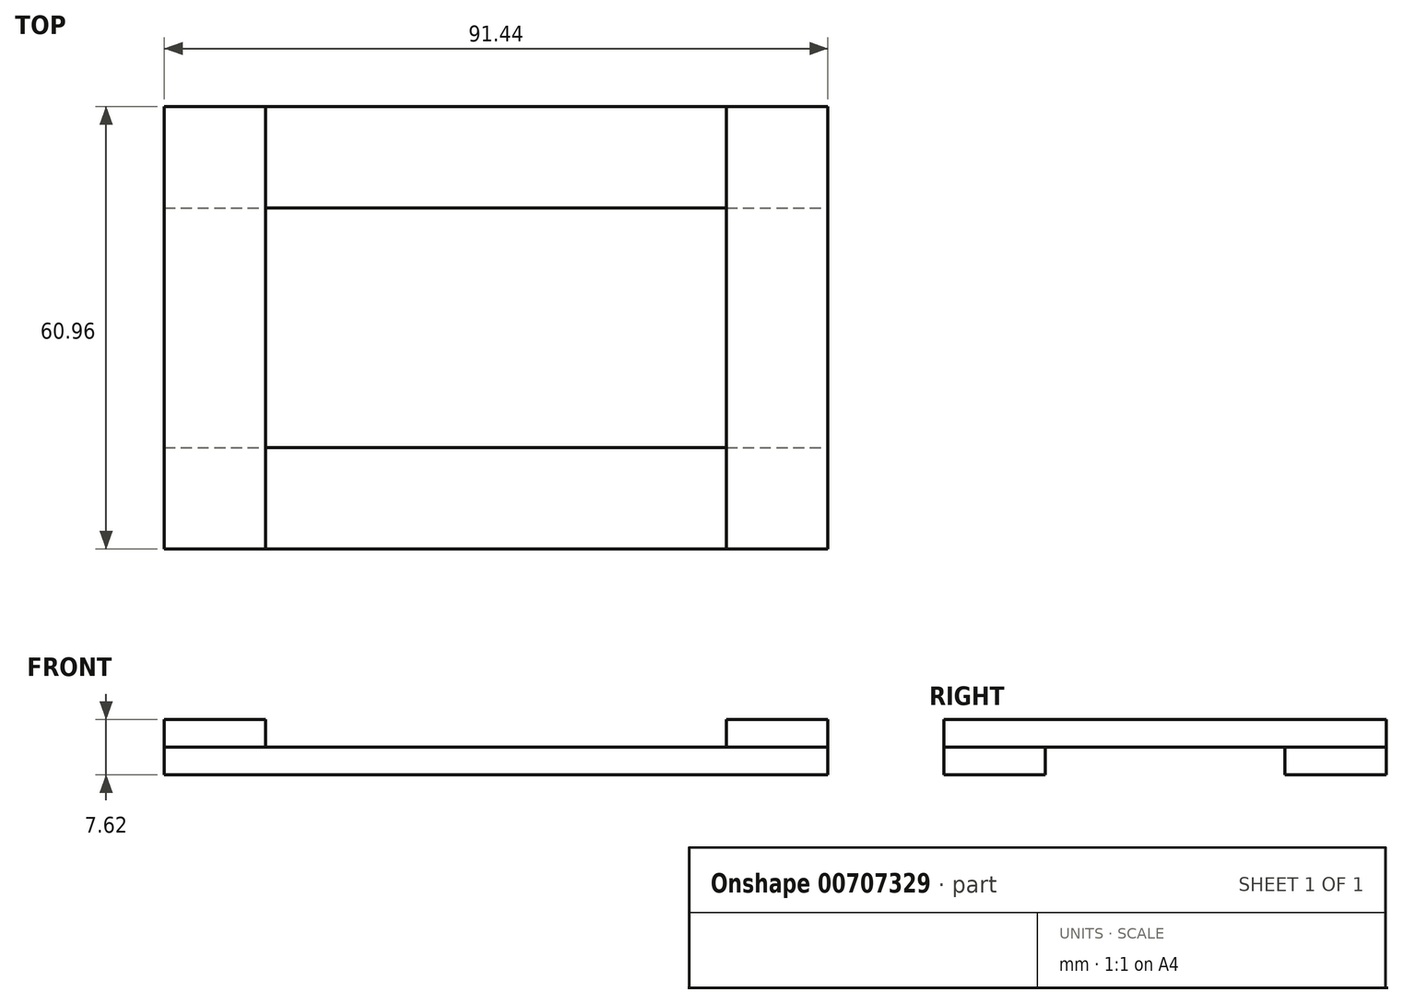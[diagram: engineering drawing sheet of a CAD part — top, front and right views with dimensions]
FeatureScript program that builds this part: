
annotation { "Feature Type Name" : "Feature", "Feature Type Description" : "" }
export const myFeature = defineFeature(function(context is Context, id is Id, definition is map)
    precondition{}
    {
        {
            var Q0;
            Q0=qCreatedBy(makeId("Top.planeOp"),FACE);
            var sketch = newSketch(context, id + "F0", { "sketchPlane" : qUnion([Q0])});
            skLineSegment(sketch, "E0.bottom", {"start": v(31.75, 66.67) * mm, "end": v(45.72, 66.67) * mm});
            skLineSegment(sketch, "E0.top", {"start": v(31.75, 5.71) * mm, "end": v(45.72, 5.71) * mm});
            skLineSegment(sketch, "E0.left", {"start": v(31.75, 66.67) * mm, "end": v(31.75, 5.71) * mm});
            skLineSegment(sketch, "E0.right", {"start": v(45.72, 66.67) * mm, "end": v(45.72, 5.71) * mm});
            skLineSegment(sketch, "E1.MirrorCS", {"start": v(-31.75, 66.67) * mm, "end": v(-45.72, 66.67) * mm});
            skLineSegment(sketch, "E2.MirrorCS", {"start": v(-31.75, 66.67) * mm, "end": v(-31.75, 5.71) * mm});
            skLineSegment(sketch, "E3.MirrorCS", {"start": v(-45.72, 66.67) * mm, "end": v(-45.72, 5.71) * mm});
            skLineSegment(sketch, "E4.MirrorCS", {"start": v(-31.75, 5.71) * mm, "end": v(-45.72, 5.71) * mm});
            skSolve(sketch);
        }
        {
            var Q0;
            Q0=makeQuery(id+"F0.imprint","IMPRINT",FACE,{"disambiguationData":[TD([[makeQuery(id+"F0.imprint","IMPRINT",EDGE,{"derivedFrom":sQuery(id+"F0.wireOp",EDGE,"E0.bottom")}),-1.0]])]});
            extrude(context, id + "F1", {"entities" : qUnion([Q0]), "depth" : 3.8 * mm, "offsetDistance" : 25.4 * mm});
        }
        {
            var Q0;
            Q0 = qSketchRegion(id + "F0", true);
            extrude(context, id + "F2", {"entities" : qUnion([Q0]), "operationType" : NewBodyOperationType.ADD, "depth" : 3.8 * mm, "offsetDistance" : 25.4 * mm});
        }
        {
            var Q0;
            Q0=sQuery(id+"F0.wireOp",EDGE,"E3.MirrorCS");
            cPoint(context, id + "F3", {"entities" : qUnion([Q0]), "parameter" : 0.5});
        }
        {
            var Q0;
            Q0=makeQuery(id+"F2.opExtrude","SWEPT_BODY",BODY,{"disambiguationData":[OSD([sQuery(id+"F0.wireOp",EDGE,"E1.MirrorCS"),sQuery(id+"F0.wireOp",EDGE,"E2.MirrorCS"),sQuery(id+"F0.wireOp",EDGE,"E3.MirrorCS"),sQuery(id+"F0.wireOp",EDGE,"E4.MirrorCS")])]});
            var Q1;
            Q1=makeQuery(id+"F1.opExtrude","SWEPT_BODY",BODY,{"disambiguationData":[OSD([sQuery(id+"F0.wireOp",EDGE,"E0.bottom"),sQuery(id+"F0.wireOp",EDGE,"E0.top"),sQuery(id+"F0.wireOp",EDGE,"E0.left"),sQuery(id+"F0.wireOp",EDGE,"E0.right")])]});
            var Q2;
            Q2 = qCreatedBy(id + "F3" ,VERTEX);
            var Q3;
            Q3=qCreatedBy(makeId("Origin.pointOp"),VERTEX);
            transform(context, id + "F4", {"entities" : qUnion([Q0, Q1]), "transformType" : TransformType.TRANSLATION_ENTITY, "oppositeDirectionEntity" : false, "transformLine" : qUnion([Q2, Q3]), "makeCopy" : false});
        }
        {
            var Q0;
            Q0=makeQuery(id+"F2.opExtrude","SWEPT_BODY",BODY,{"disambiguationData":[OSD([sQuery(id+"F0.wireOp",EDGE,"E1.MirrorCS"),sQuery(id+"F0.wireOp",EDGE,"E2.MirrorCS"),sQuery(id+"F0.wireOp",EDGE,"E3.MirrorCS"),sQuery(id+"F0.wireOp",EDGE,"E4.MirrorCS")])]});
            var Q1;
            Q1=makeQuery(id+"F1.opExtrude","SWEPT_BODY",BODY,{"disambiguationData":[OSD([sQuery(id+"F0.wireOp",EDGE,"E0.bottom"),sQuery(id+"F0.wireOp",EDGE,"E0.top"),sQuery(id+"F0.wireOp",EDGE,"E0.left"),sQuery(id+"F0.wireOp",EDGE,"E0.right")])]});
            transform(context, id + "F5", {"entities" : qUnion([Q0, Q1]), "transformType" : TransformType.TRANSLATION_3D, "dx" : -45.72 * mm, "dy" : 0 * mm, "dz" : 0 * mm, "makeCopy" : false});
        }
        {
            var Q0;
            Q0=qCreatedBy(makeId("Top.planeOp"),FACE);
            var sketch = newSketch(context, id + "F6", { "sketchPlane" : qUnion([Q0])});
            skLineSegment(sketch, "E5.bottom", {"start": v(-45.72, -30.48) * mm, "end": v(45.72, -30.48) * mm});
            skLineSegment(sketch, "E5.top", {"start": v(-45.72, -16.5) * mm, "end": v(45.72, -16.5) * mm});
            skLineSegment(sketch, "E5.left", {"start": v(-45.72, -30.48) * mm, "end": v(-45.72, -16.5) * mm});
            skLineSegment(sketch, "E5.right", {"start": v(45.72, -30.48) * mm, "end": v(45.72, -16.5) * mm});
            skLineSegment(sketch, "E6.MirrorCS", {"start": v(-45.72, 30.48) * mm, "end": v(45.72, 30.48) * mm});
            skLineSegment(sketch, "E7.MirrorCS", {"start": v(-45.72, 16.5) * mm, "end": v(45.72, 16.5) * mm});
            skLineSegment(sketch, "E8.MirrorCS", {"start": v(-45.72, 30.48) * mm, "end": v(-45.72, 16.5) * mm});
            skLineSegment(sketch, "E9.MirrorCS", {"start": v(45.72, 30.48) * mm, "end": v(45.72, 16.5) * mm});
            skSolve(sketch);
        }
        {
            var Q0;
            Q0 = qSketchRegion(id + "F6", true);
            extrude(context, id + "F7", {"entities" : qUnion([Q0]), "depth" : 3.8 * mm, "offsetDistance" : 25.4 * mm});
        }
        {
            var Q0;
            Q0=makeQuery(id+"F2.opExtrude","SWEPT_BODY",BODY,{"disambiguationData":[OSD([sQuery(id+"F0.wireOp",EDGE,"E1.MirrorCS"),sQuery(id+"F0.wireOp",EDGE,"E2.MirrorCS"),sQuery(id+"F0.wireOp",EDGE,"E3.MirrorCS"),sQuery(id+"F0.wireOp",EDGE,"E4.MirrorCS")])]});
            transform(context, id + "F8", {"entities" : qUnion([Q0]), "transformType" : TransformType.TRANSLATION_3D, "dx" : 0 * mm, "dy" : 0 * mm, "dz" : 3.8 * mm, "makeCopy" : false});
        }
        {
            var Q0;
            Q0=makeQuery(id+"F1.opExtrude","SWEPT_BODY",BODY,{"disambiguationData":[OSD([sQuery(id+"F0.wireOp",EDGE,"E0.bottom"),sQuery(id+"F0.wireOp",EDGE,"E0.top"),sQuery(id+"F0.wireOp",EDGE,"E0.left"),sQuery(id+"F0.wireOp",EDGE,"E0.right")])]});
            transform(context, id + "F9", {"entities" : qUnion([Q0]), "transformType" : TransformType.TRANSLATION_3D, "dx" : 0 * mm, "dy" : 0 * mm, "dz" : 3.8 * mm, "makeCopy" : false});
        }
    });
